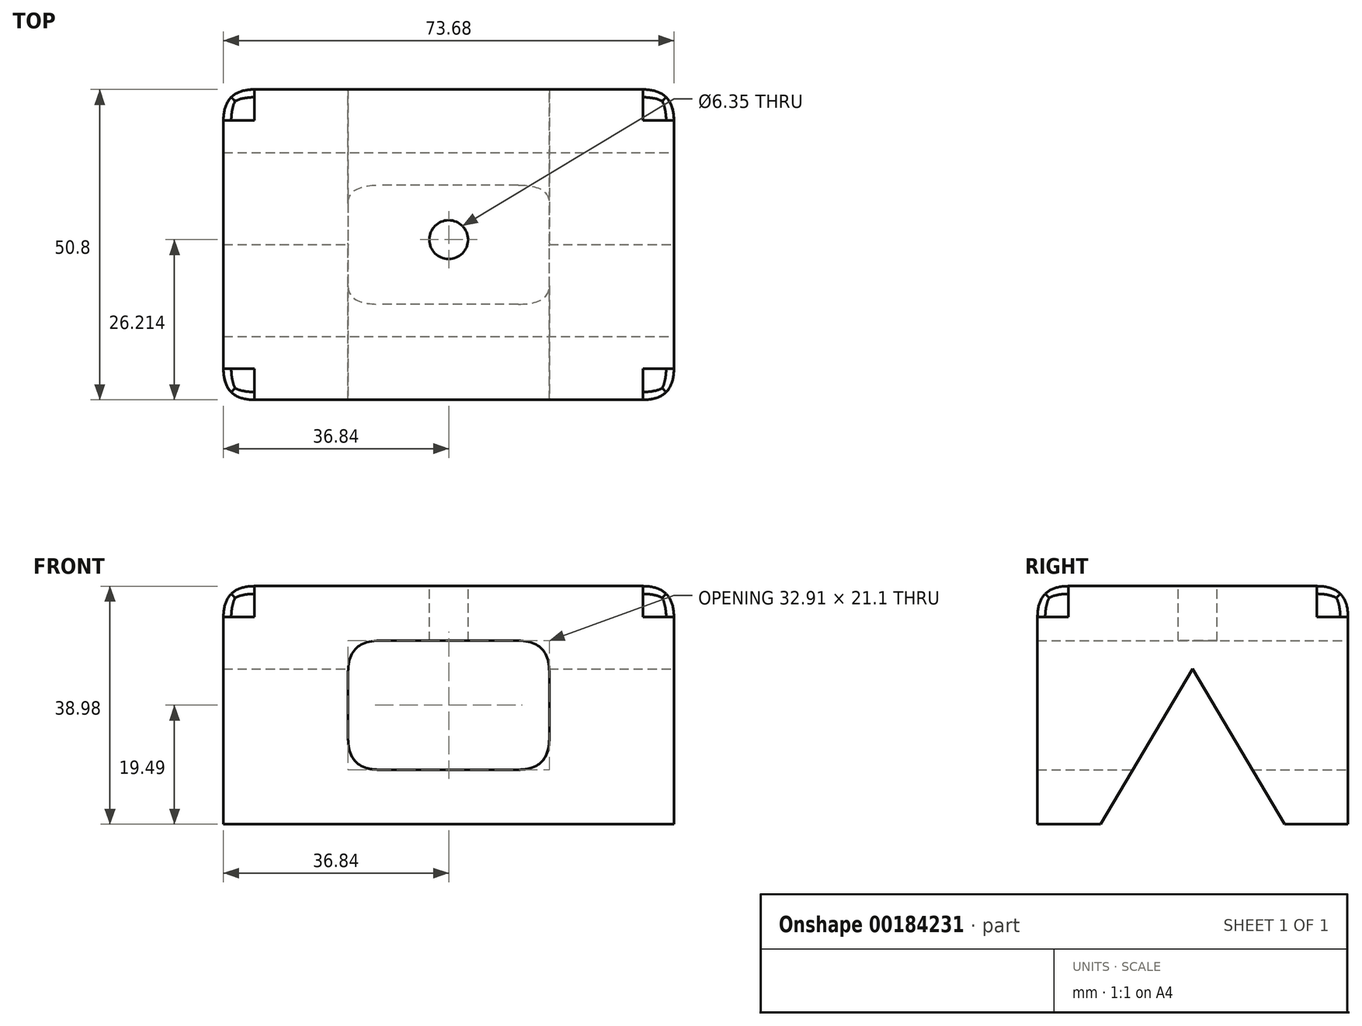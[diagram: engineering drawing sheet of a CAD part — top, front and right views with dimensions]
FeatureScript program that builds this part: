
annotation { "Feature Type Name" : "Feature", "Feature Type Description" : "" }
export const myFeature = defineFeature(function(context is Context, id is Id, definition is map)
    precondition{}
    {
        {
            var Q0;
            Q0=qCreatedBy(makeId("Front.planeOp"),FACE);
            var sketch = newSketch(context, id + "F0", { "sketchPlane" : qUnion([Q0])});
            skLineSegment(sketch, "E0.bottom", {"start": v(36.84, -19.5) * mm, "end": v(-36.84, -19.5) * mm});
            skLineSegment(sketch, "E0.top", {"start": v(36.84, 19.5) * mm, "end": v(-36.84, 19.5) * mm});
            skLineSegment(sketch, "E0.left", {"start": v(36.84, -19.5) * mm, "end": v(36.84, 19.5) * mm});
            skLineSegment(sketch, "E0.right", {"start": v(-36.84, -19.5) * mm, "end": v(-36.84, 19.5) * mm});
            skPoint(sketch, "E0.middle", {"position": v(0, 0) * mm});
            skSolve(sketch);
        }
        {
            var Q0;
            Q0 = qSketchRegion(id + "F0", true);
            extrude(context, id + "F1", {"entities" : qUnion([Q0]), "depth" : 50.8 * mm});
        }
        {
            var Q0;
            Q0=makeQuery(id+"F1.opExtrude","CAP_FACE",FACE,{"disambiguationData":[OSD([sQuery(id+"F0.wireOp",EDGE,"E0.bottom"),sQuery(id+"F0.wireOp",EDGE,"E0.top"),sQuery(id+"F0.wireOp",EDGE,"E0.left"),sQuery(id+"F0.wireOp",EDGE,"E0.right")])],"isStart":false});
            var sketch = newSketch(context, id + "F2", { "sketchPlane" : qUnion([Q0])});
            skLineSegment(sketch, "E1.bottom", {"start": v(16.45, -10.55) * mm, "end": v(-16.45, -10.55) * mm});
            skLineSegment(sketch, "E1.top", {"start": v(16.45, 10.55) * mm, "end": v(-16.45, 10.55) * mm});
            skLineSegment(sketch, "E1.left", {"start": v(16.45, -10.55) * mm, "end": v(16.45, 10.55) * mm});
            skLineSegment(sketch, "E1.right", {"start": v(-16.45, -10.55) * mm, "end": v(-16.45, 10.55) * mm});
            skPoint(sketch, "E1.middle", {"position": v(0, 0) * mm});
            skSolve(sketch);
        }
        {
            var Q0;
            Q0 = qSketchRegion(id + "F2", true);
            extrude(context, id + "F3", {"entities" : qUnion([Q0]), "operationType" : NewBodyOperationType.REMOVE, "endBound" : BoundingType.THROUGH_ALL, "oppositeDirection" : true, "depth" : 25.4 * mm});
        }
        {
            var Q0;
            Q0=makeQuery(id+"F1.opExtrude","CAP_EDGE",EDGE,{"disambiguationData":[OSD([sQuery(id+"F0.wireOp",EDGE,"E0.top")])],"isStart":false});
            var Q1;
            Q1=makeQuery(id+"F1.opExtrude","SWEPT_EDGE",EDGE,{"disambiguationData":[OSD([sQuery(id+"F0.wireOp",EDGE,"E0.top"),sQuery(id+"F0.wireOp",EDGE,"E0.right")])]});
            var Q2;
            Q2=makeQuery(id+"F1.opExtrude","CAP_EDGE",EDGE,{"disambiguationData":[OSD([sQuery(id+"F0.wireOp",EDGE,"E0.right")])],"isStart":false});
            var Q3;
            Q3=makeQuery(id+"F1.opExtrude","SWEPT_EDGE",EDGE,{"disambiguationData":[OSD([sQuery(id+"F0.wireOp",EDGE,"E0.top"),sQuery(id+"F0.wireOp",EDGE,"E0.left")])]});
            var Q4;
            Q4=makeQuery(id+"F1.opExtrude","CAP_EDGE",EDGE,{"disambiguationData":[OSD([sQuery(id+"F0.wireOp",EDGE,"E0.left")])],"isStart":false});
            var Q5;
            Q5=makeQuery(id+"F1.opExtrude","CAP_EDGE",EDGE,{"disambiguationData":[OSD([sQuery(id+"F0.wireOp",EDGE,"E0.left")])],"isStart":true});
            var Q6;
            Q6=makeQuery(id+"F1.opExtrude","CAP_EDGE",EDGE,{"disambiguationData":[OSD([sQuery(id+"F0.wireOp",EDGE,"E0.top")])],"isStart":true});
            var Q7;
            Q7=makeQuery(id+"F1.opExtrude","CAP_EDGE",EDGE,{"disambiguationData":[OSD([sQuery(id+"F0.wireOp",EDGE,"E0.right")])],"isStart":true});
            var Q8;
            Q8=makeQuery(id+"F3.boolean.opBoolean","COPY",EDGE,{"derivedFrom":makeQuery(id+"F3.opExtrude","SWEPT_EDGE",EDGE,{"disambiguationData":[OSD([sQuery(id+"F2.wireOp",EDGE,"E1.bottom"),sQuery(id+"F2.wireOp",EDGE,"E1.right")])]})});
            var Q9;
            Q9=makeQuery(id+"F3.boolean.opBoolean","COPY",EDGE,{"derivedFrom":makeQuery(id+"F3.opExtrude","SWEPT_EDGE",EDGE,{"disambiguationData":[OSD([sQuery(id+"F2.wireOp",EDGE,"E1.top"),sQuery(id+"F2.wireOp",EDGE,"E1.right")])]})});
            var Q10;
            Q10=makeQuery(id+"F3.boolean.opBoolean","COPY",EDGE,{"derivedFrom":makeQuery(id+"F3.opExtrude","SWEPT_EDGE",EDGE,{"disambiguationData":[OSD([sQuery(id+"F2.wireOp",EDGE,"E1.top"),sQuery(id+"F2.wireOp",EDGE,"E1.left")])]})});
            var Q11;
            Q11=makeQuery(id+"F3.boolean.opBoolean","COPY",EDGE,{"derivedFrom":makeQuery(id+"F3.opExtrude","SWEPT_EDGE",EDGE,{"disambiguationData":[OSD([sQuery(id+"F2.wireOp",EDGE,"E1.bottom"),sQuery(id+"F2.wireOp",EDGE,"E1.left")])]})});
            fillet(context, id + "F4", {"entities" : qUnion([Q0, Q1, Q2, Q3, Q4, Q5, Q6, Q7, Q8, Q9, Q10, Q11]), "radius" : 5.08 * mm, "tangentPropagation" : true, "rho" : 0.5, "crossSection" : FilletCrossSection.CONIC, "allowEdgeOverflow" : false});
        }
        {
            var Q0;
            Q0=makeQuery(id+"F1.opExtrude","SWEPT_FACE",FACE,{"disambiguationData":[OSD([sQuery(id+"F0.wireOp",EDGE,"E0.top")])]});
            var sketch = newSketch(context, id + "F5", { "sketchPlane" : qUnion([Q0])});
            skCircle(sketch, "E2", {"center": v(0, -24.59) * mm, "radius": 5.7 * mm});
            skSolve(sketch);
        }
        {
            var Q0;
            Q0=sQuery(id+"F5.wireOp",VERTEX,"E2.center");
            var Q1;
            Q1=makeQuery(id+"F1.opExtrude","SWEPT_BODY",BODY,{"disambiguationData":[OSD([sQuery(id+"F0.wireOp",EDGE,"E0.bottom"),sQuery(id+"F0.wireOp",EDGE,"E0.top"),sQuery(id+"F0.wireOp",EDGE,"E0.left"),sQuery(id+"F0.wireOp",EDGE,"E0.right")])]});
            hole(context, id + "F6", {"style" : HoleStyle.SIMPLE, "endStyle" : HoleEndStyle.THROUGH, "holeDiameter" : 6.35 * mm, "locations" : qUnion([Q0]), "scope" : qUnion([Q1]), "isTappedThrough" : true});
        }
        {
            var Q0;
            Q0=makeQuery(id+"F1.opExtrude","SWEPT_FACE",FACE,{"disambiguationData":[OSD([sQuery(id+"F0.wireOp",EDGE,"E0.left")])]});
            var sketch = newSketch(context, id + "F7", { "sketchPlane" : qUnion([Q0])});
            skPoint(sketch, "E3", {"position": v(-25.4, 5.9) * mm});
            skPoint(sketch, "E4", {"position": v(-25.4, -19.5) * mm});
            skLineSegment(sketch, "E5", {"start": v(-10.35, -19.5) * mm, "end": v(-40.45, -19.5) * mm});
            skLineSegment(sketch, "E6", {"start": v(-40.45, -19.5) * mm, "end": v(-25.4, 5.9) * mm});
            skLineSegment(sketch, "E7", {"start": v(-10.35, -19.5) * mm, "end": v(-25.4, 5.9) * mm});
            skSolve(sketch);
        }
        {
            var Q0;
            Q0 = qSketchRegion(id + "F7", true);
            extrude(context, id + "F8", {"entities" : qUnion([Q0]), "operationType" : NewBodyOperationType.REMOVE, "endBound" : BoundingType.THROUGH_ALL, "oppositeDirection" : true, "depth" : 25.4 * mm});
        }
    });
